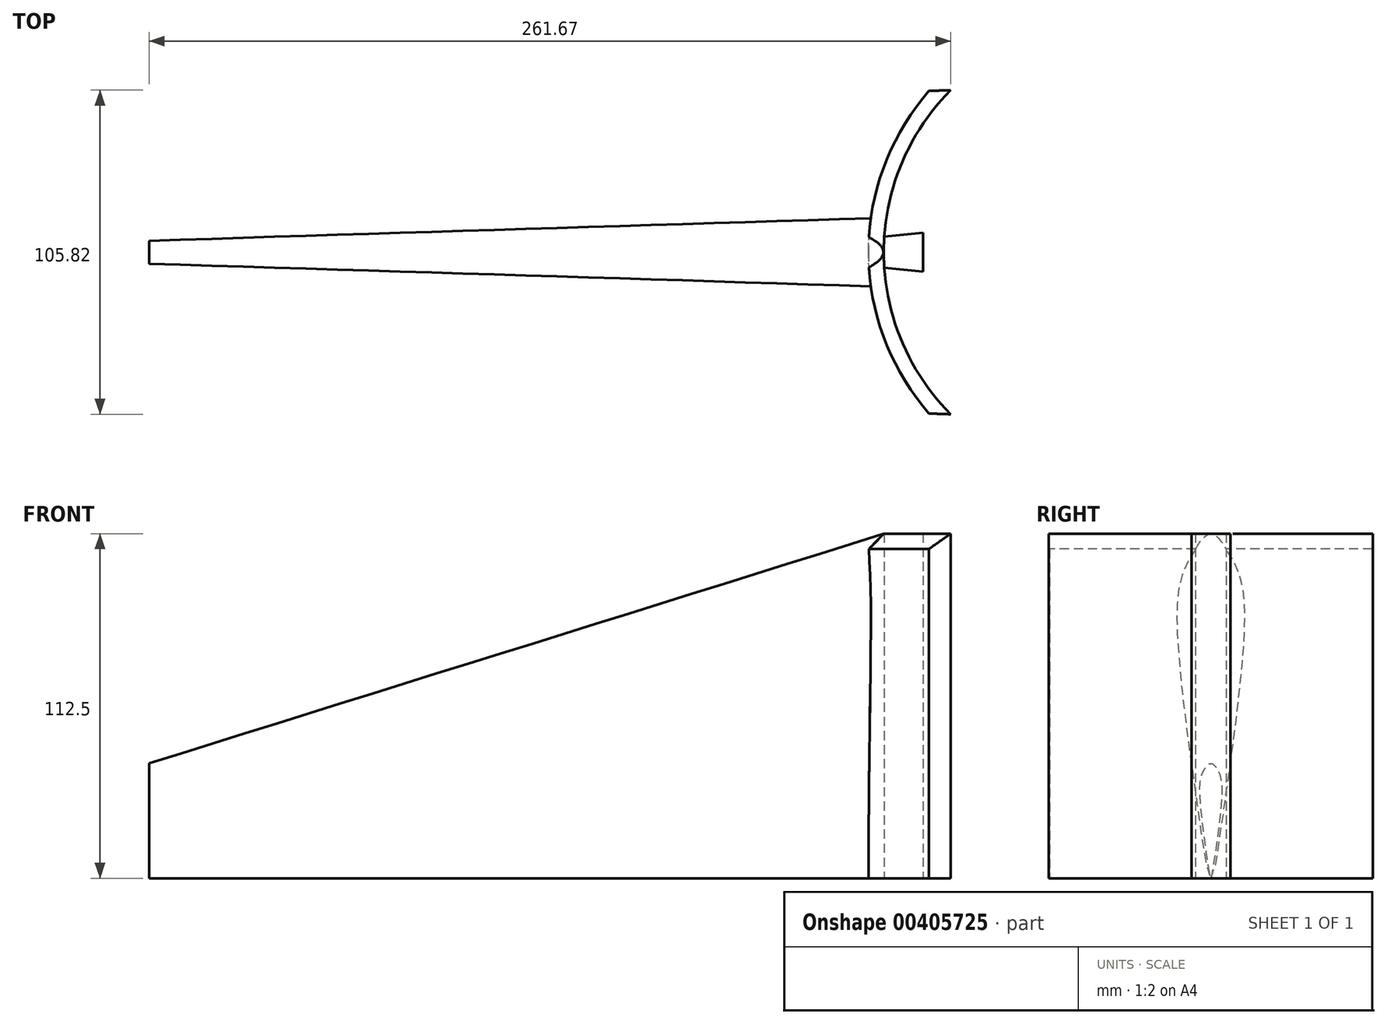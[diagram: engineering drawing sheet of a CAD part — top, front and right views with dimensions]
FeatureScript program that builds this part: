
annotation { "Feature Type Name" : "Feature", "Feature Type Description" : "" }
export const myFeature = defineFeature(function(context is Context, id is Id, definition is map)
    precondition{}
    {
        {
            var Q0;
            Q0=qCreatedBy(makeId("Top.planeOp"),FACE);
            var sketch = newSketch(context, id + "F0", { "sketchPlane" : qUnion([Q0])});
            skLineSegment(sketch, "E0", {"start": v(0, 6.35) * mm, "end": v(0, -6.35) * mm});
            skArc(sketch, "E1", {"start": v(9.2, 53.03) * mm, "mid": v(-6.05, 31.03) * mm, "end": v(-12.6, 5.06) * mm});
            skLineSegment(sketch, "E2", {"start": v(9.2, 53.03) * mm, "end": v(5.67, 56.57) * mm});
            skLineSegment(sketch, "E3.MirrorCS", {"start": v(9.2, -53.03) * mm, "end": v(5.67, -56.57) * mm});
            skArc(sketch, "E4", {"start": v(5.67, 56.57) * mm, "mid": v(-17.76, 0) * mm, "end": v(5.67, -56.57) * mm});
            skLineSegment(sketch, "E5", {"start": v(-12.6, 5.06) * mm, "end": v(0, 6.35) * mm});
            skLineSegment(sketch, "E6.MirrorCS", {"start": v(-12.6, -5.06) * mm, "end": v(0, -6.35) * mm});
            skArc(sketch, "E7.trimOffspring", {"start": v(-12.6, -5.06) * mm, "mid": v(-6.05, -31.03) * mm, "end": v(9.2, -53.03) * mm});
            skPoint(sketch, "E8", {"position": v(-17.76, 0) * mm});
            skSolve(sketch);
        }
        {
            var Q0;
            Q0=makeQuery(id+"F0.imprint","IMPRINT",FACE,{"disambiguationData":[TD([[makeQuery(id+"F0.imprint","IMPRINT",EDGE,{"derivedFrom":sQuery(id+"F0.wireOp",EDGE,"E0")}),-1.0]])]});
            extrude(context, id + "F1", {"entities" : qUnion([Q0]), "depth" : 150 * mm});
        }
        {
            var Q0;
            Q0=makeQuery(id+"F1.opExtrude","CAP_FACE",FACE,{"disambiguationData":[OSD([sQuery(id+"F0.wireOp",EDGE,"E0"),sQuery(id+"F0.wireOp",EDGE,"E1"),sQuery(id+"F0.wireOp",EDGE,"E2"),sQuery(id+"F0.wireOp",EDGE,"E3.MirrorCS"),sQuery(id+"F0.wireOp",EDGE,"E4"),sQuery(id+"F0.wireOp",EDGE,"E5"),sQuery(id+"F0.wireOp",EDGE,"E6.MirrorCS"),sQuery(id+"F0.wireOp",EDGE,"E7.trimOffspring")])],"isStart":false});
            var sketch = newSketch(context, id + "F2", { "sketchPlane" : qUnion([Q0])});
            skLineSegment(sketch, "E9", {"start": v(-12.6, 5.06) * mm, "end": v(-12.6, -5.06) * mm});
            skLineSegment(sketch, "E10", {"start": v(-12.6, -5.06) * mm, "end": v(-5.58, -3.2) * mm});
            skLineSegment(sketch, "E11", {"start": v(-5.58, -3.2) * mm, "end": v(-5.58, 3.65) * mm});
            skLineSegment(sketch, "E12", {"start": v(-5.58, 3.65) * mm, "end": v(-12.6, 5.06) * mm});
            skSolve(sketch);
        }
        {
            var Q0;
            Q0=makeQuery(id+"F2.imprint","IMPRINT",FACE,{"disambiguationData":[TD([[makeQuery(id+"F2.imprint","IMPRINT",EDGE,{"derivedFrom":sQuery(id+"F2.wireOp",EDGE,"E9")}),1.0]])]});
            extrude(context, id + "F3", {"entities" : qUnion([Q0]), "operationType" : NewBodyOperationType.ADD, "depth" : 25 * mm});
        }
        {
            var Q0;
            Q0=makeQuery(id+"F3.opExtrude","SWEPT_FACE",FACE,{"disambiguationData":[OSD([sQuery(id+"F2.wireOp",EDGE,"E9")])]});
            var sketch = newSketch(context, id + "F4", { "sketchPlane" : qUnion([Q0])});
            skPoint(sketch, "E13", {"position": v(-7.5, 142.5) * mm});
            skPoint(sketch, "E14", {"position": v(-11.25, 123.75) * mm});
            skPoint(sketch, "E15", {"position": v(-3.75, 56.25) * mm});
            skPoint(sketch, "E16", {"position": v(0, 37.5) * mm});
            skPoint(sketch, "E17", {"position": v(0, 150) * mm});
            skPoint(sketch, "E18.MirrorP", {"position": v(3.75, 56.25) * mm});
            skPoint(sketch, "E19.MirrorP", {"position": v(11.25, 123.75) * mm});
            skPoint(sketch, "E20.MirrorP", {"position": v(7.5, 142.5) * mm});
            skFitSpline(sketch, "E21", {"points": [v(0, 37.5) * mm, v(-3.75, 56.25) * mm, v(-11.25, 123.75) * mm, v(-7.5, 142.5) * mm, v(0, 150) * mm, v(7.5, 142.5) * mm, v(11.25, 123.75) * mm, v(3.75, 56.25) * mm, v(0, 37.5) * mm]});
            skSolve(sketch);
        }
        {
            var Q0;
            {var subQ0=sQuery(id+"F2.wireOp",EDGE,"E9");Q0=makeQuery(id+"F4.imprint","IMPRINT",FACE,{"disambiguationData":[TD([[makeQuery(id+"F4.imprint","IMPRINT",EDGE,{"derivedFrom":makeQuery(id+"F3.opExtrude","CAP_EDGE",EDGE,{"disambiguationData":[OSD([subQ0])],"isStart":false})}),-1.0]])]});}
            var sketch = newSketch(context, id + "F5", { "sketchPlane" : qUnion([Q0])});
            skLineSegment(sketch, "E22.bottom", {"start": v(-4.23, 173.8) * mm, "end": v(4, 173.8) * mm});
            skLineSegment(sketch, "E22.top", {"start": v(-4.23, 166.76) * mm, "end": v(4, 166.76) * mm});
            skLineSegment(sketch, "E22.left", {"start": v(-4.23, 173.8) * mm, "end": v(-4.23, 166.76) * mm});
            skLineSegment(sketch, "E22.right", {"start": v(4, 173.8) * mm, "end": v(4, 166.76) * mm});
            skSolve(sketch);
        }
        {
            var Q0;
            Q0=makeQuery(id+"F5.imprint","IMPRINT",FACE,{"disambiguationData":[TD([[makeQuery(id+"F5.imprint","IMPRINT",EDGE,{"derivedFrom":sQuery(id+"F5.wireOp",EDGE,"E22.bottom")}),-1.0]])]});
            extrude(context, id + "F6", {"entities" : qUnion([Q0]), "operationType" : NewBodyOperationType.ADD, "depth" : 240 * mm});
        }
        {
            var Q0;
            Q0=makeQuery(id+"F6.opExtrude","CAP_FACE",FACE,{"disambiguationData":[OSD([sQuery(id+"F5.wireOp",EDGE,"E22.bottom"),sQuery(id+"F5.wireOp",EDGE,"E22.top"),sQuery(id+"F5.wireOp",EDGE,"E22.left"),sQuery(id+"F5.wireOp",EDGE,"E22.right")])],"isStart":false});
            var sketch = newSketch(context, id + "F7", { "sketchPlane" : qUnion([Q0])});
            skPoint(sketch, "E23", {"position": v(-2.5, 72.5) * mm});
            skPoint(sketch, "E24", {"position": v(-3.75, 66.25) * mm});
            skPoint(sketch, "E25", {"position": v(-1.25, 43.75) * mm});
            skPoint(sketch, "E26", {"position": v(0, 75) * mm});
            skPoint(sketch, "E27", {"position": v(0, 37.5) * mm});
            skPoint(sketch, "E28.MirrorP", {"position": v(1.25, 43.75) * mm});
            skPoint(sketch, "E29.MirrorP", {"position": v(3.75, 66.25) * mm});
            skPoint(sketch, "E30.MirrorP", {"position": v(2.5, 72.5) * mm});
            skFitSpline(sketch, "E31", {"points": [v(0, 37.5) * mm, v(-1.25, 43.75) * mm, v(-3.75, 66.25) * mm, v(-2.5, 72.5) * mm, v(0, 75) * mm, v(2.5, 72.5) * mm, v(3.75, 66.25) * mm, v(1.25, 43.75) * mm, v(0, 37.5) * mm]});
            skSolve(sketch);
        }
        {
            var Q1;
            Q1 = qSketchRegion(id + "F4", true);
            var Q2;
            Q2 = qSketchRegion(id + "F7", true);
            loft(context, id + "F8", {"operationType" : NewBodyOperationType.ADD, "sheetProfilesArray" : [{ "sheetProfileEntities" : qUnion([Q1]) }, { "sheetProfileEntities" : qUnion([Q2]) }]});
        }
        {
            var Q0;
            Q0=makeQuery(id+"F3.opExtrude","SWEPT_FACE",FACE,{"disambiguationData":[OSD([sQuery(id+"F2.wireOp",EDGE,"E11")])]});
            var sketch = newSketch(context, id + "F9", { "sketchPlane" : qUnion([Q0])});
            skLineSegment(sketch, "E32", {"start": v(11.42, 150) * mm, "end": v(14.16, 153.86) * mm});
            skLineSegment(sketch, "E33", {"start": v(11.42, 150) * mm, "end": v(-11.4, 150) * mm});
            skLineSegment(sketch, "E34", {"start": v(-11.4, 150) * mm, "end": v(-13.7, 171.85) * mm});
            skLineSegment(sketch, "E35", {"start": v(-13.7, 171.85) * mm, "end": v(-7.09, 176.17) * mm});
            skLineSegment(sketch, "E36", {"start": v(-7.09, 176.17) * mm, "end": v(15.74, 176.17) * mm});
            skLineSegment(sketch, "E37", {"start": v(15.74, 176.17) * mm, "end": v(14.16, 153.86) * mm});
            skSolve(sketch);
        }
        {
            var Q0;
            {var subQ5=sQuery(id+"F9.wireOp",EDGE,"E32");Q0=makeQuery(id+"F9.imprint","IMPRINT",FACE,{"disambiguationData":[TD([[makeQuery(id+"F9.imprint","IMPRINT",EDGE,{"derivedFrom":subQ5}),1.0]])]});}
            var Q1;
            {var subQ1=sQuery(id+"F2.wireOp",EDGE,"E11");Q1=makeQuery(id+"F9.imprint","IMPRINT",FACE,{"disambiguationData":[TD([[makeQuery(id+"F9.imprint","IMPRINT",EDGE,{"derivedFrom":makeQuery(id+"F3.opExtrude","CAP_EDGE",EDGE,{"disambiguationData":[OSD([subQ1])],"isStart":false})}),-1.0]])]});}
            extrude(context, id + "F10", {"entities" : qUnion([Q0, Q1]), "operationType" : NewBodyOperationType.REMOVE, "oppositeDirection" : true, "depth" : 304 * mm});
        }
        {
            var Q0;
            Q0=makeQuery(id+"F1.opExtrude","SWEPT_EDGE",EDGE,{"disambiguationData":[OSD([sQuery(id+"F0.wireOp",EDGE,"E3.MirrorCS"),sQuery(id+"F0.wireOp",EDGE,"E4")])]});
            var Q1;
            Q1=makeQuery(id+"F1.opExtrude","SWEPT_EDGE",EDGE,{"disambiguationData":[OSD([sQuery(id+"F0.wireOp",EDGE,"E2"),sQuery(id+"F0.wireOp",EDGE,"E4")])]});
            var Q2;
            Q2=makeQuery(id+"F1.opExtrude","CAP_EDGE",EDGE,{"disambiguationData":[OSD([sQuery(id+"F0.wireOp",EDGE,"E4")])],"isStart":false});
            chamfer(context, id + "F11", {"entities" : qUnion([Q0, Q1, Q2]), "width" : 5 * mm, "tangentPropagation" : true});
        }
        {
            var Q0;
            Q0=qCreatedBy(makeId("Top.planeOp"),FACE);
            var sketch = newSketch(context, id + "F12", { "sketchPlane" : qUnion([Q0])});
            skLineSegment(sketch, "E38.bottom", {"start": v(-60.06, -72.2) * mm, "end": v(51.4, -72.2) * mm});
            skLineSegment(sketch, "E38.top", {"start": v(-60.06, 64.66) * mm, "end": v(51.4, 64.66) * mm});
            skLineSegment(sketch, "E38.left", {"start": v(-60.06, -72.2) * mm, "end": v(-60.06, 64.66) * mm});
            skLineSegment(sketch, "E38.right", {"start": v(51.4, -72.2) * mm, "end": v(51.4, 64.66) * mm});
            skSolve(sketch);
        }
        {
            var Q0;
            Q0=makeQuery(id+"F12.imprint","IMPRINT",FACE,{"disambiguationData":[TD([[makeQuery(id+"F12.imprint","IMPRINT",EDGE,{"derivedFrom":sQuery(id+"F12.wireOp",EDGE,"E38.bottom")}),1.0]])]});
            extrude(context, id + "F13", {"entities" : qUnion([Q0]), "operationType" : NewBodyOperationType.REMOVE, "depth" : 37.5 * mm});
        }
    });
